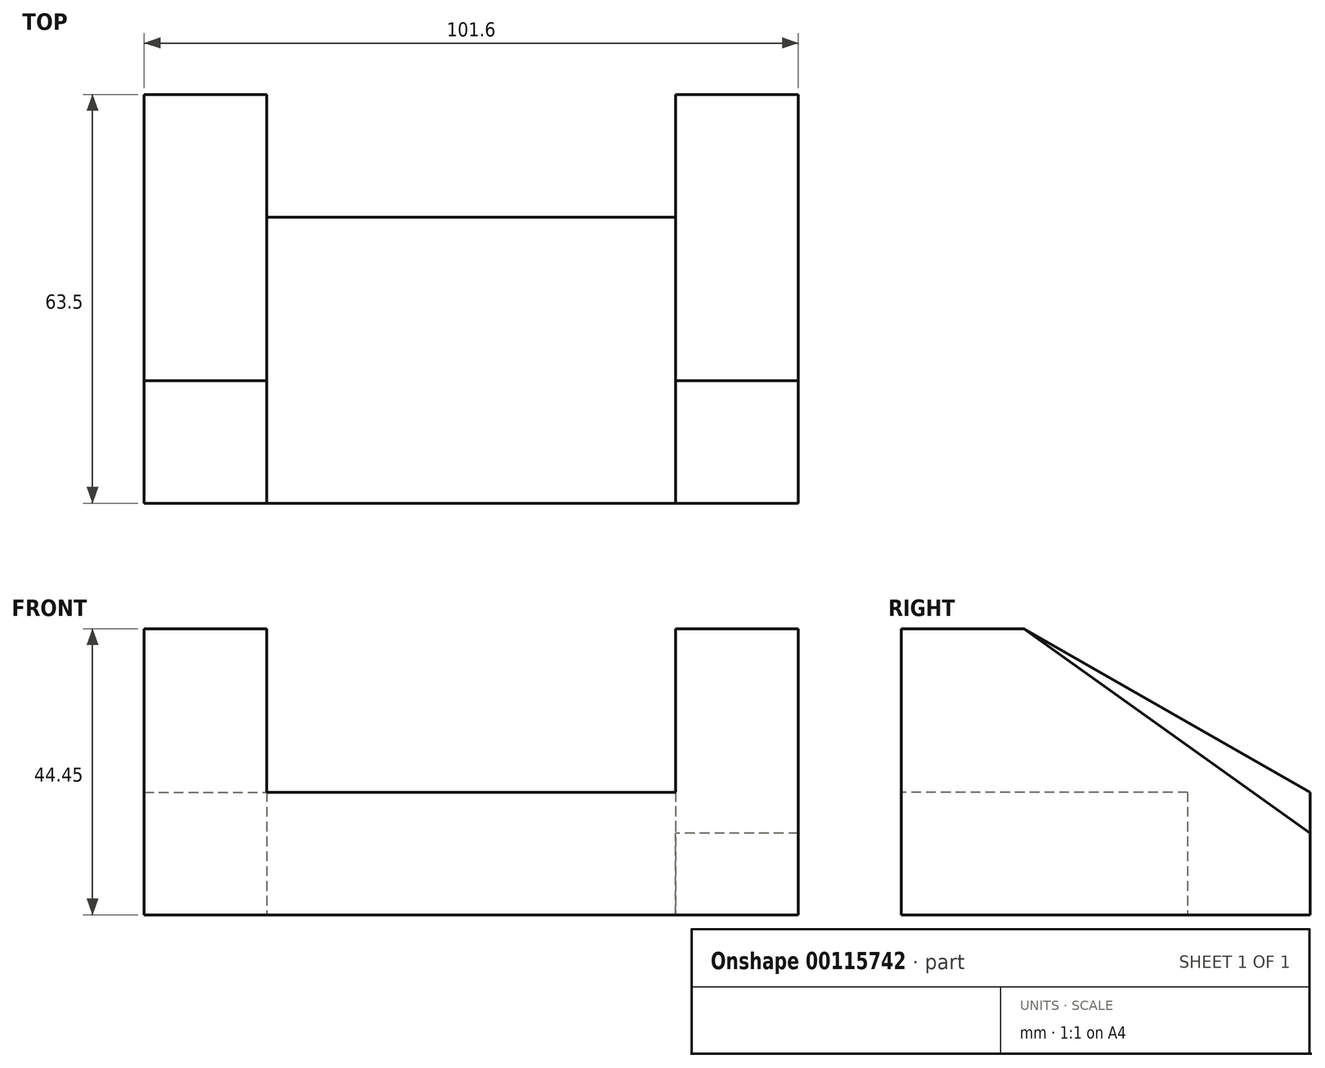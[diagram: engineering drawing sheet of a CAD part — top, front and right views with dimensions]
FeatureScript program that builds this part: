
annotation { "Feature Type Name" : "Feature", "Feature Type Description" : "" }
export const myFeature = defineFeature(function(context is Context, id is Id, definition is map)
    precondition{}
    {
        {
            var Q0;
            Q0=qCreatedBy(makeId("Top.planeOp"),FACE);
            var sketch = newSketch(context, id + "F0", { "sketchPlane" : qUnion([Q0])});
            skLineSegment(sketch, "E0", {"start": v(0, 0) * mm, "end": v(-63.5, 0) * mm});
            skLineSegment(sketch, "E1", {"start": v(-63.5, 0) * mm, "end": v(-63.5, 44.45) * mm});
            skLineSegment(sketch, "E2", {"start": v(-63.5, 44.45) * mm, "end": v(0, 44.45) * mm});
            skLineSegment(sketch, "E3", {"start": v(0, 44.45) * mm, "end": v(0, 0) * mm});
            skSolve(sketch);
        }
        {
            var Q0;
            Q0=makeQuery(id+"F0.imprint","IMPRINT",FACE,{"disambiguationData":[TD([[makeQuery(id+"F0.imprint","IMPRINT",EDGE,{"derivedFrom":sQuery(id+"F0.wireOp",EDGE,"E0")}),-1.0]])]});
            extrude(context, id + "F1", {"entities" : qUnion([Q0]), "depth" : 19.05 * mm});
        }
        {
            var Q0;
            Q0=qCreatedBy(makeId("Right.planeOp"),FACE);
            var sketch = newSketch(context, id + "F2", { "sketchPlane" : qUnion([Q0])});
            skLineSegment(sketch, "E4", {"start": v(0, 0) * mm, "end": v(63.5, 0) * mm});
            skLineSegment(sketch, "E5", {"start": v(0, 0) * mm, "end": v(0, 44.45) * mm});
            skLineSegment(sketch, "E6", {"start": v(63.5, 0) * mm, "end": v(63.5, 12.7) * mm});
            skLineSegment(sketch, "E7", {"start": v(0, 44.45) * mm, "end": v(19.05, 44.45) * mm});
            skLineSegment(sketch, "E8", {"start": v(19.05, 44.45) * mm, "end": v(63.5, 12.7) * mm});
            skSolve(sketch);
        }
        {
            var Q0;
            Q0=makeQuery(id+"F2.imprint","IMPRINT",FACE,{"disambiguationData":[TD([[makeQuery(id+"F2.imprint","IMPRINT",EDGE,{"derivedFrom":sQuery(id+"F2.wireOp",EDGE,"E4")}),1.0]])]});
            extrude(context, id + "F3", {"entities" : qUnion([Q0]), "operationType" : NewBodyOperationType.ADD, "depth" : 19.05 * mm});
        }
        {
            var Q0;
            Q0=makeQuery(id+"F1.opExtrude","SWEPT_FACE",FACE,{"disambiguationData":[OSD([sQuery(id+"F0.wireOp",EDGE,"E1")])]});
            var sketch = newSketch(context, id + "F4", { "sketchPlane" : qUnion([Q0])});
            skLineSegment(sketch, "E9", {"start": v(0, 0) * mm, "end": v(0, 44.45) * mm});
            skPoint(sketch, "E9.endSnap0", {"position": v(0, 9.53) * mm});
            skLineSegment(sketch, "E10", {"start": v(0, 0) * mm, "end": v(-63.5, 0) * mm});
            skLineSegment(sketch, "E11", {"start": v(-63.5, 0) * mm, "end": v(-63.5, 19.05) * mm});
            skLineSegment(sketch, "E12", {"start": v(0, 44.45) * mm, "end": v(-19.05, 44.45) * mm});
            skLineSegment(sketch, "E13", {"start": v(-19.05, 44.45) * mm, "end": v(-63.5, 19.05) * mm});
            skSolve(sketch);
        }
        {
            var Q0;
            {var subQ5=sQuery(id+"F4.wireOp",EDGE,"E11");Q0=makeQuery(id+"F4.imprint","IMPRINT",FACE,{"disambiguationData":[TD([[makeQuery(id+"F4.imprint","IMPRINT",EDGE,{"derivedFrom":subQ5}),-1.0]])]});}
            var Q1;
            {var subQ3=sQuery(id+"F0.wireOp",EDGE,"E1");var subQ4=makeQuery(id+"F1.opExtrude","CAP_EDGE",EDGE,{"disambiguationData":[OSD([subQ3])],"isStart":false});Q1=makeQuery(id+"F4.imprint","IMPRINT",FACE,{"disambiguationData":[TD([[makeQuery(id+"F4.imprint","IMPRINT",EDGE,{"derivedFrom":subQ4}),1.0]])]});}
            extrude(context, id + "F5", {"entities" : qUnion([Q0, Q1]), "operationType" : NewBodyOperationType.ADD, "depth" : 19.05 * mm});
        }
    });
